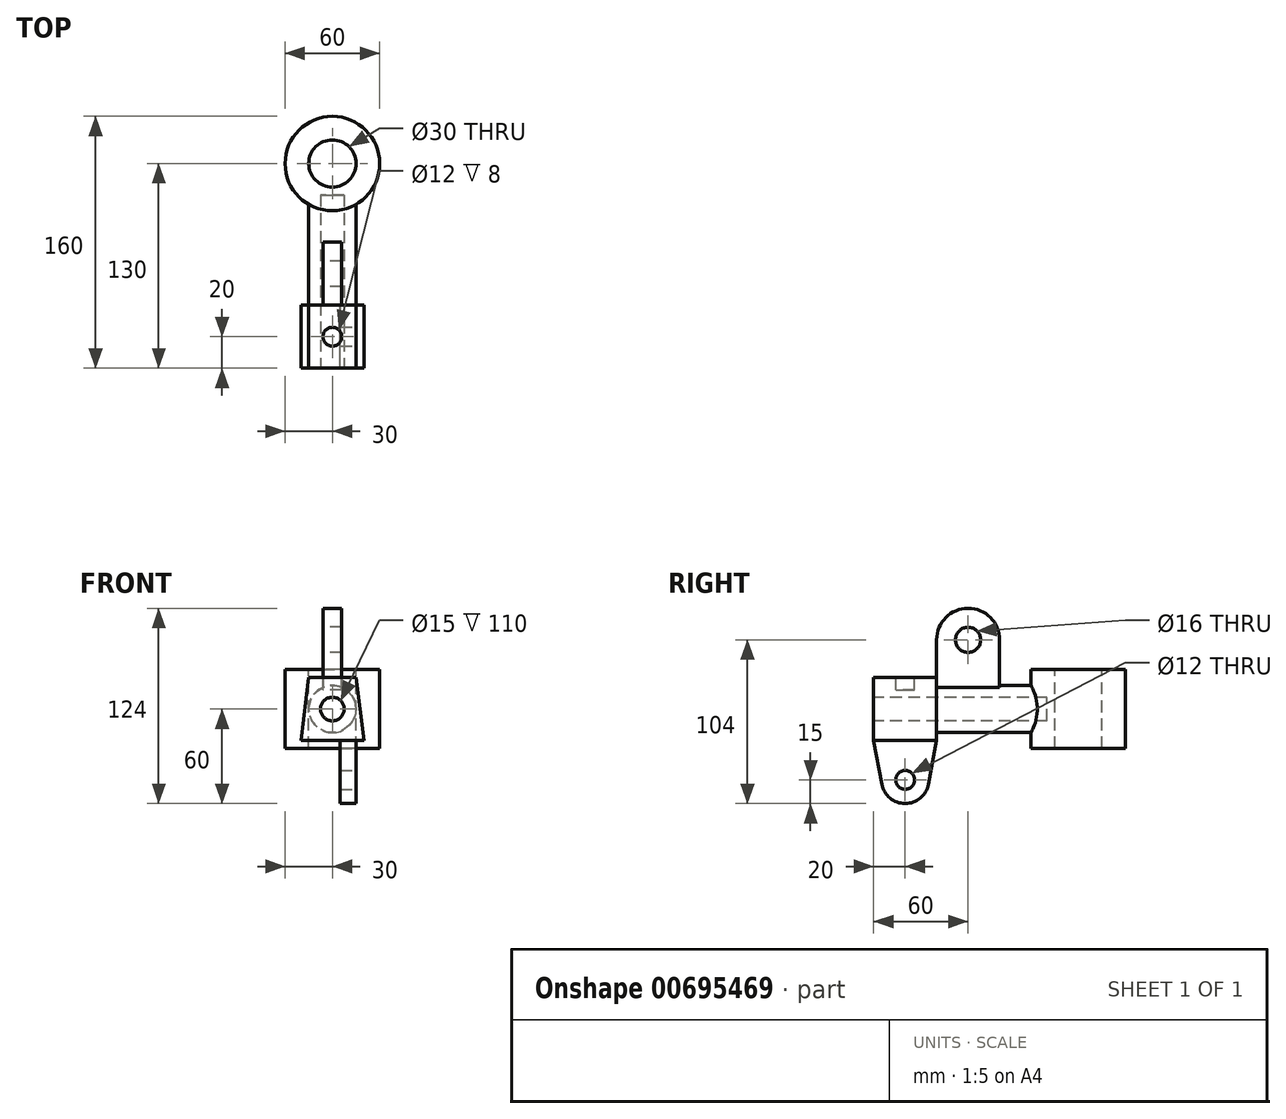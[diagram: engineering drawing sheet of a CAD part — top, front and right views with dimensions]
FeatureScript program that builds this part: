
annotation { "Feature Type Name" : "Feature", "Feature Type Description" : "" }
export const myFeature = defineFeature(function(context is Context, id is Id, definition is map)
    precondition{}
    {
        {
            var Q0;
            Q0=qCreatedBy(makeId("Front.planeOp"),FACE);
            var sketch = newSketch(context, id + "F0", { "sketchPlane" : qUnion([Q0])});
            skCircle(sketch, "E0", {"center": v(0, 0) * mm, "radius": 15 * mm, "construction": true});
            skLineSegment(sketch, "E1", {"start": v(-15, 20) * mm, "end": v(15, 20) * mm});
            skLineSegment(sketch, "E2", {"start": v(-20, -20) * mm, "end": v(20, -20) * mm});
            skLineSegment(sketch, "E3", {"start": v(-20, -20) * mm, "end": v(-15, 20) * mm});
            skLineSegment(sketch, "E4", {"start": v(15, 20) * mm, "end": v(20, -20) * mm});
            skSolve(sketch);
        }
        {
            var Q0;
            Q0=makeQuery(id+"F0.imprint","IMPRINT",FACE,{"disambiguationData":[TD([[makeQuery(id+"F0.imprint","IMPRINT",EDGE,{"derivedFrom":sQuery(id+"F0.wireOp",EDGE,"E1")}),-1.0]])]});
            extrude(context, id + "F1", {"entities" : qUnion([Q0]), "oppositeDirection" : true, "depth" : 40 * mm, "offsetDistance" : 25 * mm});
        }
        {
            var Q0;
            Q0=makeQuery(id+"F1.opExtrude","CAP_FACE",FACE,{"disambiguationData":[OSD([sQuery(id+"F0.wireOp",EDGE,"E1"),sQuery(id+"F0.wireOp",EDGE,"E2"),sQuery(id+"F0.wireOp",EDGE,"E3"),sQuery(id+"F0.wireOp",EDGE,"E4")])],"isStart":false});
            var sketch = newSketch(context, id + "F2", { "sketchPlane" : qUnion([Q0])});
            skCircle(sketch, "E5", {"center": v(0, 0) * mm, "radius": 15 * mm});
            skSolve(sketch);
        }
        {
            var Q0;
            Q0=makeQuery(id+"F2.imprint","IMPRINT",FACE,{"disambiguationData":[TD([[makeQuery(id+"F2.imprint","IMPRINT",EDGE,{"derivedFrom":sQuery(id+"F2.wireOp",EDGE,"E5")}),1.0]])]});
            extrude(context, id + "F3", {"entities" : qUnion([Q0]), "operationType" : NewBodyOperationType.ADD, "depth" : 90 * mm, "offsetDistance" : 25 * mm});
        }
        {
            var Q0;
            Q0=qCreatedBy(makeId("Top.planeOp"),FACE);
            var sketch = newSketch(context, id + "F4", { "sketchPlane" : qUnion([Q0])});
            skCircle(sketch, "E6", {"center": v(0, 130) * mm, "radius": 30 * mm});
            skSolve(sketch);
        }
        {
            var Q0;
            Q0=makeQuery(id+"F4.imprint","IMPRINT",FACE,{"disambiguationData":[TD([[makeQuery(id+"F4.imprint","IMPRINT",EDGE,{"derivedFrom":sQuery(id+"F4.wireOp",EDGE,"E6")}),1.0]])]});
            extrude(context, id + "F5", {"entities" : qUnion([Q0]), "operationType" : NewBodyOperationType.ADD, "depth" : 50 * mm, "offsetDistance" : 25 * mm, "symmetric" : true});
        }
        {
            var Q0;
            Q0=qCreatedBy(makeId("Right.planeOp"),FACE);
            var sketch = newSketch(context, id + "F6", { "sketchPlane" : qUnion([Q0])});
            skCircle(sketch, "E7", {"center": v(60, 44) * mm, "radius": 8 * mm});
            skLineSegment(sketch, "E8.0", {"start": v(40, 20) * mm, "end": v(40, -20) * mm, "construction": true});
            skLineSegment(sketch, "E9", {"start": v(40, 10.44) * mm, "end": v(40, 44) * mm});
            skArc(sketch, "E10", {"start": v(80, 44) * mm, "mid": v(60, 64) * mm, "end": v(40, 44) * mm});
            skLineSegment(sketch, "E11", {"start": v(80, 44) * mm, "end": v(80, 6.84) * mm});
            skLineSegment(sketch, "E12", {"start": v(80, 6.84) * mm, "end": v(40, 6.84) * mm});
            skLineSegment(sketch, "E13", {"start": v(40, 6.84) * mm, "end": v(40, 10.44) * mm});
            skSolve(sketch);
        }
        {
            var Q0;
            Q0=makeQuery(id+"F6.imprint","IMPRINT",FACE,{"disambiguationData":[TD([[makeQuery(id+"F6.imprint","IMPRINT",EDGE,{"derivedFrom":sQuery(id+"F6.wireOp",EDGE,"E7")}),-1.0]])]});
            extrude(context, id + "F7", {"entities" : qUnion([Q0]), "operationType" : NewBodyOperationType.ADD, "depth" : 12 * mm, "offsetDistance" : 25 * mm, "symmetric" : true});
        }
        {
            var Q0;
            Q0=qCreatedBy(makeId("Right.planeOp"),FACE);
            cPlane(context, id + "F8", {"entities" : qUnion([Q0]), "cplaneType" : CPlaneType.OFFSET, "offset" : 15 * mm, "width" : 150 * mm, "height" : 150 * mm});
        }
        {
            var Q0;
            Q0=qCreatedBy(id+"F8.planeOp",FACE);
            var sketch = newSketch(context, id + "F9", { "sketchPlane" : qUnion([Q0])});
            skPoint(sketch, "E14.0", {"position": v(0, -20) * mm});
            skPoint(sketch, "E14.1", {"position": v(40, -20) * mm});
            skPoint(sketch, "E15.0", {"position": v(20, -20) * mm});
            skLineSegment(sketch, "E16", {"start": v(20, 22.87) * mm, "end": v(20, -64.8) * mm, "construction": true});
            skArc(sketch, "E17", {"start": v(5.26, -47.8) * mm, "mid": v(20, -60) * mm, "end": v(34.74, -47.8) * mm});
            skLineSegment(sketch, "E18", {"start": v(0, -20) * mm, "end": v(40, -20) * mm});
            skLineSegment(sketch, "E19", {"start": v(40, -20) * mm, "end": v(34.74, -47.8) * mm});
            skLineSegment(sketch, "E20", {"start": v(0, -20) * mm, "end": v(5.26, -47.8) * mm});
            skSolve(sketch);
        }
        {
            var Q0;
            Q0=makeQuery(id+"F9.imprint","IMPRINT",FACE,{"disambiguationData":[TD([[makeQuery(id+"F9.imprint","IMPRINT",EDGE,{"derivedFrom":sQuery(id+"F9.wireOp",EDGE,"E17")}),1.0]])]});
            extrude(context, id + "F10", {"entities" : qUnion([Q0]), "operationType" : NewBodyOperationType.ADD, "oppositeDirection" : true, "depth" : 10 * mm, "offsetDistance" : 25 * mm});
        }
        {
            var Q0;
            Q0=makeQuery(id+"F10.opExtrude","CAP_FACE",FACE,{"disambiguationData":[OSD([sQuery(id+"F9.wireOp",EDGE,"E17"),sQuery(id+"F9.wireOp",EDGE,"E18"),sQuery(id+"F9.wireOp",EDGE,"E19"),sQuery(id+"F9.wireOp",EDGE,"E20")])],"isStart":true});
            var sketch = newSketch(context, id + "F11", { "sketchPlane" : qUnion([Q0])});
            skCircle(sketch, "E21", {"center": v(20, -45) * mm, "radius": 6 * mm});
            skSolve(sketch);
        }
        {
            var Q0;
            Q0=makeQuery(id+"F11.imprint","IMPRINT",FACE,{"disambiguationData":[TD([[makeQuery(id+"F11.imprint","IMPRINT",EDGE,{"derivedFrom":sQuery(id+"F11.wireOp",EDGE,"E21")}),1.0]])]});
            var Q1;
            Q1=makeQuery(id+"F10.opExtrude","CAP_FACE",FACE,{"disambiguationData":[OSD([sQuery(id+"F9.wireOp",EDGE,"E17"),sQuery(id+"F9.wireOp",EDGE,"E18"),sQuery(id+"F9.wireOp",EDGE,"E19"),sQuery(id+"F9.wireOp",EDGE,"E20")])],"isStart":false});
            extrude(context, id + "F12", {"entities" : qUnion([Q0]), "operationType" : NewBodyOperationType.REMOVE, "endBound" : BoundingType.UP_TO_SURFACE, "oppositeDirection" : true, "depth" : 25 * mm, "endBoundEntityFace" : qUnion([Q1]), "offsetDistance" : 25 * mm});
        }
        {
            var Q0;
            Q0=makeQuery(id+"F5.opExtrude","CAP_FACE",FACE,{"disambiguationData":[OSD([sQuery(id+"F4.wireOp",EDGE,"E6")])],"isStart":false});
            var sketch = newSketch(context, id + "F13", { "sketchPlane" : qUnion([Q0])});
            skCircle(sketch, "E22", {"center": v(0, 130) * mm, "radius": 15 * mm});
            skSolve(sketch);
        }
        {
            var Q0;
            Q0=makeQuery(id+"F13.imprint","IMPRINT",FACE,{"disambiguationData":[TD([[makeQuery(id+"F13.imprint","IMPRINT",EDGE,{"derivedFrom":sQuery(id+"F13.wireOp",EDGE,"E22")}),1.0]])]});
            extrude(context, id + "F14", {"entities" : qUnion([Q0]), "operationType" : NewBodyOperationType.REMOVE, "endBound" : BoundingType.THROUGH_ALL, "oppositeDirection" : true, "depth" : 25 * mm, "offsetDistance" : 25 * mm});
        }
        {
            var Q0;
            Q0=makeQuery(id+"F1.opExtrude","SWEPT_FACE",FACE,{"disambiguationData":[OSD([sQuery(id+"F0.wireOp",EDGE,"E1")])]});
            var sketch = newSketch(context, id + "F15", { "sketchPlane" : qUnion([Q0])});
            skCircle(sketch, "E23", {"center": v(0, 20) * mm, "radius": 6 * mm});
            skPoint(sketch, "E23.centerSnap0", {"position": v(0, 40) * mm});
            skSolve(sketch);
        }
        {
            var Q0;
            Q0=makeQuery(id+"F15.imprint","IMPRINT",FACE,{"disambiguationData":[TD([[makeQuery(id+"F15.imprint","IMPRINT",EDGE,{"derivedFrom":sQuery(id+"F15.wireOp",EDGE,"E23")}),1.0]])]});
            extrude(context, id + "F16", {"entities" : qUnion([Q0]), "operationType" : NewBodyOperationType.REMOVE, "oppositeDirection" : true, "depth" : 8 * mm, "offsetDistance" : 25 * mm});
        }
        {
            var Q0;
            Q0=makeQuery(id+"F0.imprint","IMPRINT",FACE,{"disambiguationData":[TD([[makeQuery(id+"F0.imprint","IMPRINT",EDGE,{"derivedFrom":sQuery(id+"F0.wireOp",EDGE,"E1")}),-1.0]])]});
            var sketch = newSketch(context, id + "F17", { "sketchPlane" : qUnion([Q0])});
            skCircle(sketch, "E24", {"center": v(0, 0) * mm, "radius": 7.5 * mm});
            skSolve(sketch);
        }
        {
            var Q0;
            Q0=makeQuery(id+"F17.imprint","IMPRINT",FACE,{"disambiguationData":[TD([[makeQuery(id+"F17.imprint","IMPRINT",EDGE,{"derivedFrom":sQuery(id+"F17.wireOp",EDGE,"E24")}),1.0]])]});
            extrude(context, id + "F18", {"entities" : qUnion([Q0]), "operationType" : NewBodyOperationType.REMOVE, "oppositeDirection" : true, "depth" : 110 * mm, "offsetDistance" : 25 * mm});
        }
    });
